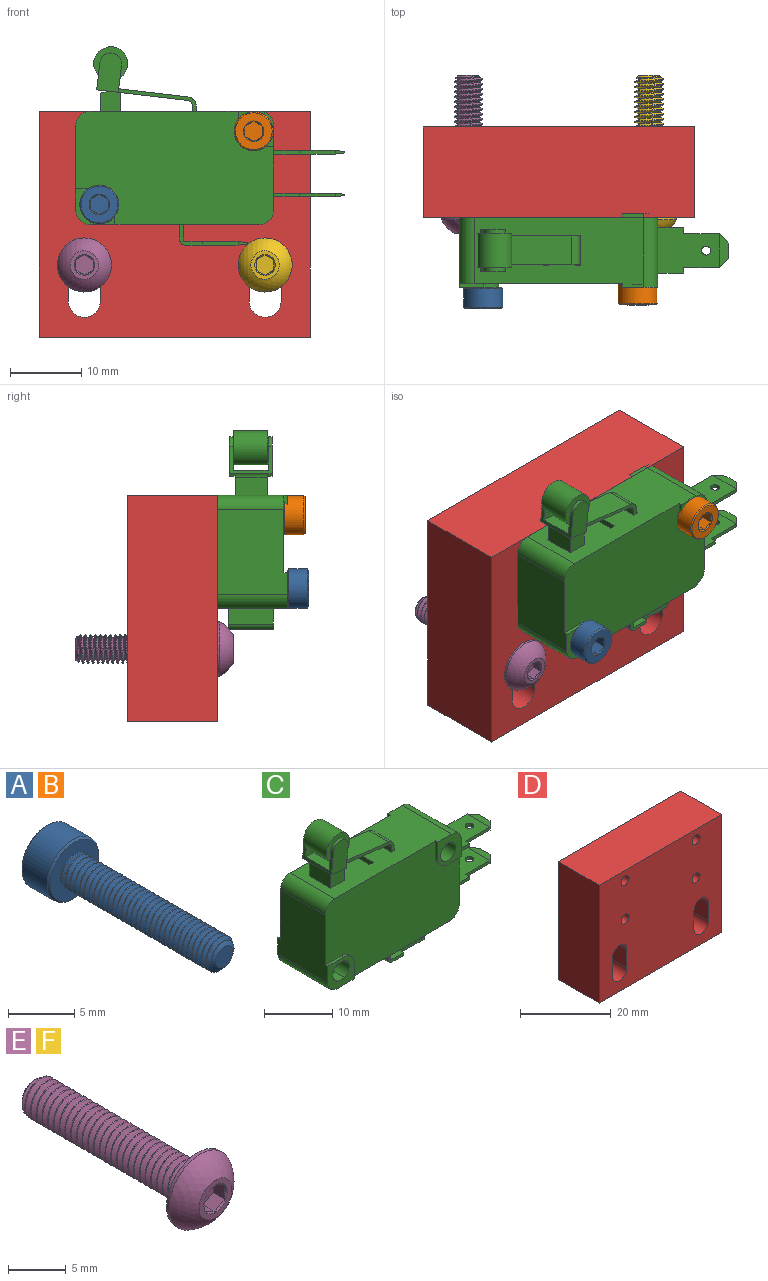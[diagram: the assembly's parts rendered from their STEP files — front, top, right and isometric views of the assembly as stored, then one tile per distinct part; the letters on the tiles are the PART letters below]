
ASSEMBLY  parts=6 mates=5
PART A: 57 faces, bbox 6x19.6x6 mm
  f0: cylinder r=1.5mm len=3mm, axis (0,-1,0), area 0.3mm2, adj f1,f32,f33,f35,f36
  f1: cylinder r=1.5mm len=3mm, axis (0,-1,0), area 0.6mm2, adj f0,f2,f32,f33
  f2: cylinder r=1.5mm len=3mm, axis (0,-1,0), area 0.6mm2, adj f1,f3,f32,f33
  f3: cylinder r=1.5mm len=3mm, axis (0,-1,0), area 0.6mm2, adj f2,f4,f32,f33
  f4: cylinder r=1.5mm len=3mm, axis (0,-1,0), area 0.6mm2, adj f3,f5,f32,f33
  f5: cylinder r=1.5mm len=3mm, axis (0,-1,0), area 0.6mm2, adj f4,f6,f32,f33
  f6: cylinder r=1.5mm len=3mm, axis (0,-1,0), area 0.6mm2, adj f5,f7,f32,f33
  f7: cylinder r=1.5mm len=3mm, axis (0,-1,0), area 0.6mm2, adj f6,f8,f32,f33
  f8: cylinder r=1.5mm len=3mm, axis (0,-1,0), area 0.6mm2, adj f7,f9,f32,f33
  f9: cylinder r=1.5mm len=3mm, axis (0,-1,0), area 0.6mm2, adj f8,f10,f32,f33
  f10: cylinder r=1.5mm len=3mm, axis (0,-1,0), area 0.6mm2, adj f9,f11,f32,f33
  f11: cylinder r=1.5mm len=3mm, axis (0,-1,0), area 0.6mm2, adj f10,f12,f32,f33
  f12: cylinder r=1.5mm len=3mm, axis (0,-1,0), area 0.6mm2, adj f11,f13,f32,f33
  f13: cylinder r=1.5mm len=3mm, axis (0,-1,0), area 0.6mm2, adj f12,f14,f32,f33
  f14: cylinder r=1.5mm len=3mm, axis (0,-1,0), area 0.6mm2, adj f13,f15,f32,f33
  f15: cylinder r=1.5mm len=3mm, axis (0,-1,0), area 0.6mm2, adj f14,f16,f32,f33
  f16: cylinder r=1.5mm len=3mm, axis (0,-1,0), area 0.6mm2, adj f15,f17,f32,f33
  f17: cylinder r=1.5mm len=3mm, axis (0,-1,0), area 0.6mm2, adj f16,f18,f32,f33
  f18: cylinder r=1.5mm len=3mm, axis (0,-1,0), area 0.6mm2, adj f17,f19,f32,f33
  f19: cylinder r=1.5mm len=3mm, axis (0,-1,0), area 0.6mm2, adj f18,f20,f32,f33
  f20: cylinder r=1.5mm len=3mm, axis (0,-1,0), area 0.6mm2, adj f19,f21,f32,f33
  f21: cylinder r=1.5mm len=3mm, axis (0,-1,0), area 0.6mm2, adj f20,f22,f32,f33
  f22: cylinder r=1.5mm len=3mm, axis (0,-1,0), area 0.6mm2, adj f21,f23,f32,f33
  f23: cylinder r=1.5mm len=3mm, axis (0,-1,0), area 0.6mm2, adj f22,f24,f32,f33
  f24: cylinder r=1.5mm len=3mm, axis (0,-1,0), area 0.6mm2, adj f23,f25,f32,f33
  f25: cylinder r=1.5mm len=3mm, axis (0,-1,0), area 0.6mm2, adj f24,f26,f32,f33
  f26: cylinder r=1.5mm len=3mm, axis (0,-1,0), area 0.6mm2, adj f25,f27,f32,f33
  f27: cylinder r=1.5mm len=3mm, axis (0,-1,0), area 0.6mm2, adj f26,f28,f32,f33
  f28: cylinder r=1.5mm len=3mm, axis (0,-1,0), area 0.6mm2, adj f27,f29,f32,f33
  f29: cylinder r=1.5mm len=3mm, axis (0,-1,0), area 0.6mm2, adj f28,f30,f32,f33
  f30: cylinder r=1.5mm len=3mm, axis (0,-1,0), area 0.6mm2, adj f29,f31,f32,f33
  f31: cylinder r=1.5mm len=3mm, axis (0,-1,0), area 1.4mm2, adj f30,f32,f33,f40,f56
  f32: bspline ~16.1x3.46mm, area 97.9mm2, adj f0,f1,f2,f3,f4,f5,f6,f7
  f33: bspline ~15.85x3.46mm, area 97.9mm2, adj f0,f1,f2,f3,f4,f5,f6,f7
  f34: cylinder r=1.18mm len=15.56mm, axis (0,1,0), area 26.7mm2, adj f32,f33,f35,f56
  f35: cone r=0.92mm half-angle=55deg, axis (0,1,0), area 3.5mm2, adj f0,f32,f34,f36,f37
  f36: cone r=0.92mm half-angle=55deg, axis (0,1,0), area 0.1mm2, adj f0,f33,f35
  f37: plane 1.84x1.84mm, normal (0,-1,0), area 2.7mm2, adj f35
  f38: cylinder r=2.75mm len=5.5mm, axis (0,-1,0), area 46.1mm2, adj f54,f55
  f39: plane 5.17x5.17mm, normal (0,1,0), area 14.4mm2, adj f41,f42,f43,f44,f45,f46,f54
  f40: plane 5.17x5.17mm, normal (0,-1,0), area 13.9mm2, adj f31,f55
  f41: cone r=1.44mm half-angle=45deg, axis (0,1,0), area 0mm2, adj f39,f48
  f42: cone r=1.44mm half-angle=45deg, axis (0,1,0), area 0mm2, adj f39,f49
  f43: cone r=1.44mm half-angle=45deg, axis (0,1,0), area 0mm2, adj f39,f50
  f44: cone r=1.44mm half-angle=45deg, axis (0,1,0), area 0mm2, adj f39,f51
  f45: cone r=1.44mm half-angle=45deg, axis (0,1,0), area 0mm2, adj f39,f52
  f46: cone r=1.44mm half-angle=45deg, axis (0,1,0), area 0mm2, adj f39,f53
  f47: plane 2.89x2.5mm, normal (0,1,0), area 5.4mm2, adj f48,f49,f50,f51,f52,f53
  f48: plane 2.42x1.8mm, normal (-0.5,0,-0.87), area 2.5mm2, adj f41,f47,f49,f53
  f49: plane 2.42x1.99mm, normal (-1,0,0), area 2.5mm2, adj f42,f47,f48,f50
  f50: plane 2.42x1.8mm, normal (-0.5,0,0.87), area 2.5mm2, adj f43,f47,f49,f51
  f51: plane 2.42x1.8mm, normal (0.5,0,0.87), area 2.5mm2, adj f44,f47,f50,f52
  f52: plane 2.42x1.99mm, normal (1,0,0), area 2.5mm2, adj f45,f47,f51,f53
  f53: plane 2.42x1.8mm, normal (0.5,0,-0.87), area 2.5mm2, adj f46,f47,f48,f52
  f54: cone r=2.58mm half-angle=45deg, axis (0,-1,0), area 3.9mm2, adj f38,f39
  f55: cone r=2.75mm half-angle=45deg, axis (0,1,0), area 3.9mm2, adj f38,f40
  f56: cone r=1.5mm half-angle=67.5deg, axis (0,1,0), area 1.5mm2, adj f31,f32,f33,f34
PART B: same geometry as A
PART C: 124 faces, bbox 37.8x10.3x27.9 mm
  f0: cylinder r=0.64mm len=1.27mm, axis (0,0,1), area 2mm2, adj f84,f85
  f1: cylinder r=0.64mm len=1.27mm, axis (0,0,1), area 2mm2, adj f73,f74
  f2: cylinder r=0.64mm len=1.27mm, axis (0,0,1), area 2mm2, adj f51,f53
  f3: cylinder r=1.7mm len=10.31mm, axis (0,1,0), area 40.2mm2, adj f6,f11,f13,f15
  f4: cylinder r=1.55mm len=10.31mm, axis (0,1,0), area 100.4mm2, adj f5,f12
  f5: plane 5x5mm, normal (0,1,0), area 15.6mm2, adj f4,f9,f10,f19,f42,f43,f44
  f6: plane 5.5x5mm, normal (0,1,0), area 16.8mm2, adj f3,f7,f8,f13,f14,f15,f16,f45
  f7: plane 11.9x10.31mm, normal (-1,0,0), area 113.8mm2, adj f6,f11,f16,f18,f37,f41,f45,f48
  f8: plane 23.8x10.31mm, normal (0,0,-1), area 221.9mm2, adj f6,f11,f16,f17,f35,f41,f47,f48
  f9: plane 11.9x10.31mm, normal (1,0,0), area 107.3mm2, adj f5,f12,f17,f19,f40,f41,f42,f48
  f10: plane 23.8x10.31mm, normal (0,0,1), area 205.5mm2, adj f5,f12,f18,f19,f20,f21,f22,f23
  f11: plane 5.5x5mm, normal (0,-1,0), area 16.8mm2, adj f3,f7,f8,f13,f14,f15,f16,f35
  f12: plane 5x5mm, normal (0,-1,0), area 15.6mm2, adj f4,f9,f10,f19,f38,f39,f40
  f13: plane 10.31x1.4mm, normal (0,0,1), area 14.4mm2, adj f3,f6,f11,f14
  f14: cylinder r=1.7mm len=10.31mm, axis (0,1,0), area 40.2mm2, adj f6,f11,f13,f15
  f15: plane 10.31x1.4mm, normal (0,0,-1), area 14.4mm2, adj f3,f6,f11,f14
  f16: cylinder r=2mm len=10.31mm, axis (0,1,0), area 32.4mm2, adj f6,f7,f8,f11
  f17: cylinder r=2mm len=9.31mm, axis (0,1,0), area 29.2mm2, adj f8,f9,f41,f48
  f18: cylinder r=2mm len=9.31mm, axis (0,1,0), area 29.2mm2, adj f7,f10,f41,f48
  f19: cylinder r=2mm len=10.31mm, axis (0,1,0), area 32.4mm2, adj f5,f9,f10,f12
  f20: plane 2.85x2mm, normal (0,1,0), area 4.4mm2, adj f10,f21,f23,f24,f115,f116,f117
  f21: plane 4.25x2mm, normal (1,0,0), area 8.5mm2, adj f10,f20,f22,f24
  f22: plane 2.85x2mm, normal (0,-1,0), area 5.7mm2, adj f10,f21,f23,f24
  f23: plane 4.25x2mm, normal (-1,0,0), area 8.5mm2, adj f10,f20,f22,f24
  f24: plane 4.25x2.85mm, normal (0,0,1), area 12.1mm2, adj f20,f21,f22,f23
  f25: plane 4.25x2mm, normal (1,0,0), area 8.5mm2, adj f10,f26,f28,f29
  f26: plane 2x0.76mm, normal (0,-1,0), area 1.5mm2, adj f10,f25,f27,f29
  f27: plane 4.25x2mm, normal (-1,0,0), area 8.5mm2, adj f10,f26,f28,f29
  f28: plane 2x0.76mm, normal (0,1,0), area 1.5mm2, adj f10,f25,f27,f29
  f29: plane 4.25x0.76mm, normal (0,0,1), area 3.2mm2, adj f25,f26,f27,f28
  f30: plane 4.25x2mm, normal (1,0,0), area 8.5mm2, adj f10,f31,f33,f34
  f31: plane 2x0.76mm, normal (0,-1,0), area 1.5mm2, adj f10,f30,f32,f34
  f32: plane 4.25x2mm, normal (-1,0,0), area 8.5mm2, adj f10,f31,f33,f34
  f33: plane 2x0.76mm, normal (0,1,0), area 1.5mm2, adj f10,f30,f32,f34
  f34: plane 4.25x0.76mm, normal (0,0,1), area 3.2mm2, adj f30,f31,f32,f33
  f35: plane 2.8x0.5mm, normal (1,0,0), area 1.4mm2, adj f8,f11,f36,f41
  f36: cylinder r=2.2mm len=2.2mm, axis (0,-1,0), area 1.7mm2, adj f11,f35,f37,f41
  f37: plane 3.3x0.5mm, normal (0,0,1), area 1.6mm2, adj f7,f11,f36,f41
  f38: plane 2.8x0.5mm, normal (-1,0,0), area 1.4mm2, adj f10,f12,f39,f41
  f39: cylinder r=2.2mm len=2.2mm, axis (0,-1,0), area 1.7mm2, adj f12,f38,f40,f41
  f40: plane 2.8x0.5mm, normal (0,0,-1), area 1.4mm2, adj f9,f12,f39,f41
  f41: plane 27.8x15.9mm, normal (0,-1,0), area 389.9mm2, adj f7,f8,f9,f10,f17,f18,f35,f36
  f42: plane 2.8x0.5mm, normal (0,0,-1), area 1.4mm2, adj f5,f9,f43,f48
  f43: cylinder r=2.2mm len=2.2mm, axis (0,1,0), area 1.7mm2, adj f5,f42,f44,f48
  f44: plane 2.8x0.5mm, normal (-1,0,0), area 1.4mm2, adj f5,f10,f43,f48
  f45: plane 3.3x0.5mm, normal (0,0,1), area 1.6mm2, adj f6,f7,f46,f48
  f46: cylinder r=2.2mm len=2.2mm, axis (0,1,0), area 1.7mm2, adj f6,f45,f47,f48
  f47: plane 2.8x0.5mm, normal (1,0,0), area 1.4mm2, adj f6,f8,f46,f48
  f48: plane 27.8x15.9mm, normal (0,1,0), area 389.9mm2, adj f7,f8,f9,f10,f17,f18,f42,f43
  f49: plane 6.35x2.19mm, normal (-1,0,0), area 13.9mm2, adj f8,f50,f56,f57
  f50: cylinder r=0.71mm len=6.35mm, axis (0,1,0), area 7.1mm2, adj f49,f51,f56,f57
  f51: plane 7.48x6.35mm, normal (0,0,-1), area 38.1mm2, adj f2,f50,f56,f57,f59,f60,f61,f63
  f52: plane 2.12x0.17mm, normal (1,0,0), area 0.4mm2, adj f58,f62,f86,f87
  f53: plane 7.48x6.35mm, normal (0,0,1), area 38.1mm2, adj f2,f54,f56,f57,f59,f60,f61,f63
  f54: cylinder r=0.2mm len=6.35mm, axis (0,1,0), area 2mm2, adj f53,f55,f56,f57
  f55: plane 6.35x2.19mm, normal (1,0,0), area 13.9mm2, adj f8,f54,f56,f57
  f56: plane 3.15x2.9mm, normal (0,-1,0), area 2.7mm2, adj f8,f49,f50,f51,f53,f54,f55,f63
  f57: plane 3.15x2.9mm, normal (0,1,0), area 2.7mm2, adj f8,f49,f50,f51,f53,f54,f55,f60
  f58: plane 1.32x1.32mm, normal (0.71,0.71,0), area 0.6mm2, adj f52,f59,f86,f87
  f59: plane 5.03x0.51mm, normal (0,1,0), area 2.6mm2, adj f51,f53,f58,f60
  f60: plane 0.8x0.51mm, normal (1,0,0), area 0.4mm2, adj f51,f53,f57,f59
  f61: plane 5.03x0.51mm, normal (0,-1,0), area 2.6mm2, adj f51,f53,f62,f63
  f62: plane 1.32x1.32mm, normal (0.71,-0.71,0), area 0.6mm2, adj f52,f61,f86,f87
  f63: plane 0.8x0.51mm, normal (1,0,0), area 0.4mm2, adj f51,f53,f56,f61
  f64: plane 3.65x0.51mm, normal (0,1,0), area 1.9mm2, adj f9,f65,f73,f74
  f65: plane 0.8x0.51mm, normal (1,0,0), area 0.4mm2, adj f64,f66,f73,f74
  f66: plane 5.03x0.51mm, normal (0,1,0), area 2.6mm2, adj f65,f67,f73,f74
  f67: plane 1.32x1.32mm, normal (0.71,0.71,0), area 0.6mm2, adj f66,f68,f88,f89
  f68: plane 2.12x0.17mm, normal (1,0,0), area 0.4mm2, adj f67,f69,f88,f89
  f69: plane 1.32x1.32mm, normal (0.71,-0.71,0), area 0.6mm2, adj f68,f70,f88,f89
  f70: plane 5.03x0.51mm, normal (0,-1,0), area 2.6mm2, adj f69,f71,f73,f74
  f71: plane 0.8x0.51mm, normal (1,0,0), area 0.4mm2, adj f70,f72,f73,f74
  f72: plane 3.65x0.51mm, normal (0,-1,0), area 1.9mm2, adj f9,f71,f73,f74
  f73: plane 8.68x6.35mm, normal (0,0,-1), area 45.8mm2, adj f1,f9,f64,f65,f66,f70,f71,f72
  f74: plane 8.68x6.35mm, normal (0,0,1), area 45.8mm2, adj f1,f9,f64,f65,f66,f70,f71,f72
  f75: plane 3.65x0.51mm, normal (0,1,0), area 1.9mm2, adj f9,f76,f84,f85
  f76: plane 0.8x0.51mm, normal (1,0,0), area 0.4mm2, adj f75,f77,f84,f85
  f77: plane 5.03x0.51mm, normal (0,1,0), area 2.6mm2, adj f76,f78,f84,f85
  f78: plane 1.32x1.32mm, normal (0.71,0.71,0), area 0.6mm2, adj f77,f79,f90,f91
  f79: plane 2.12x0.17mm, normal (1,0,0), area 0.4mm2, adj f78,f80,f90,f91
  f80: plane 1.32x1.32mm, normal (0.71,-0.71,0), area 0.6mm2, adj f79,f81,f90,f91
  f81: plane 5.03x0.51mm, normal (0,-1,0), area 2.6mm2, adj f80,f82,f84,f85
  f82: plane 0.8x0.51mm, normal (1,0,0), area 0.4mm2, adj f81,f83,f84,f85
  f83: plane 3.65x0.51mm, normal (0,-1,0), area 1.9mm2, adj f9,f82,f84,f85
  f84: plane 8.68x6.35mm, normal (0,0,-1), area 45.8mm2, adj f0,f9,f75,f76,f77,f81,f82,f83
  f85: plane 8.68x6.35mm, normal (0,0,1), area 45.8mm2, adj f0,f9,f75,f76,f77,f81,f82,f83
  f86: plane 4.75x1.32mm, normal (0.13,0,0.99), area 4.6mm2, adj f52,f53,f58,f62
  f87: plane 4.75x1.32mm, normal (0.13,0,-0.99), area 4.6mm2, adj f51,f52,f58,f62
  f88: plane 4.75x1.32mm, normal (0.13,0,0.99), area 4.6mm2, adj f67,f68,f69,f74
  f89: plane 4.75x1.32mm, normal (0.13,0,-0.99), area 4.6mm2, adj f67,f68,f69,f73
  f90: plane 4.75x1.32mm, normal (0.13,0,0.99), area 4.6mm2, adj f78,f79,f80,f85
  f91: plane 4.75x1.32mm, normal (0.13,0,-0.99), area 4.6mm2, adj f78,f79,f80,f84
  f92: plane 2.8x2.8mm, normal (0,-1,0), area 7.6mm2, adj f10,f93,f112,f113,f116,f117
  f93: plane 12.76x6mm, normal (-0.12,0,-0.99), area 53.8mm2, adj f92,f100,f101,f103,f104,f106,f108,f110
  f94: cylinder r=0.38mm len=0.76mm, axis (0,1,0), area 1.3mm2, adj f104,f107
  f95: cylinder r=1.52mm len=3.04mm, axis (0,-1,0), area 2.7mm2, adj f100,f103,f105,f106
  f96: plane 12.76x4.88mm, normal (0.12,0,0.99), area 54.7mm2, adj f99,f100,f105,f106,f107,f108,f110,f111
  f97: plane 4.06x0.51mm, normal (0,0,-1), area 2.1mm2, adj f98,f102,f110,f111
  f98: plane 4.06x1.21mm, normal (1,0,0), area 4.9mm2, adj f97,f99,f110,f111
  f99: cylinder r=1.3mm len=4.06mm, axis (0,1,0), area 7.7mm2, adj f96,f98,f110,f111
  f100: plane 6x3.83mm, normal (-0.99,0,0.12), area 6.8mm2, adj f93,f95,f96,f103,f104,f105,f107,f109
  f101: cylinder r=0.79mm len=4.06mm, axis (0,1,0), area 4.7mm2, adj f93,f102,f110,f111
  f102: plane 4.06x1.21mm, normal (-1,0,0), area 4.9mm2, adj f97,f101,f110,f111
  f103: plane 5.53x3.49mm, normal (0,-1,0), area 15.4mm2, adj f93,f95,f100,f106
  f104: plane 5.53x3.49mm, normal (0,1,0), area 15mm2, adj f93,f94,f100,f108,f109
  f105: plane 5.03x3.43mm, normal (0,1,0), area 12.9mm2, adj f95,f96,f100,f106,f123
  f106: plane 3.83x0.97mm, normal (0.99,0,-0.12), area 2.4mm2, adj f93,f95,f96,f103,f105,f111
  f107: plane 5.03x3.43mm, normal (0,-1,0), area 13.4mm2, adj f94,f96,f100,f108,f109
  f108: plane 3.83x0.97mm, normal (0.99,0,-0.12), area 2.4mm2, adj f93,f96,f104,f107,f109,f110
  f109: cylinder r=1.52mm len=3.04mm, axis (0,1,0), area 2.7mm2, adj f100,f104,f107,f108
  f110: plane 10.94x3.65mm, normal (0,1,0), area 6.4mm2, adj f93,f96,f97,f98,f99,f101,f102,f108
  f111: plane 10.94x3.65mm, normal (0,-1,0), area 6.4mm2, adj f93,f96,f97,f98,f99,f101,f102,f106
  f112: cylinder r=4mm len=4.4mm, axis (0,1,0), area 2.1mm2, adj f92,f93,f114,f116
  f113: cylinder r=4mm len=4.4mm, axis (0,1,0), area 6.2mm2, adj f92,f93,f114,f117
  f114: plane 3.25x2.8mm, normal (0,1,0), area 8.9mm2, adj f93,f112,f113,f115,f116,f117
  f115: plane 4.23x2.8mm, normal (0,0,-1), area 11.8mm2, adj f20,f114,f116,f117
  f116: plane 4.4x3mm, normal (1,0,0), area 13.1mm2, adj f10,f20,f92,f112,f114,f115
  f117: plane 4.4x3mm, normal (-1,0,0), area 13.1mm2, adj f10,f20,f92,f113,f114,f115
  f118: plane 0.71x0.71mm, normal (0,1,0), area 0.4mm2, adj f122
  f119: plane 4.8x4.8mm, normal (0,1,0), area 17.7mm2, adj f121,f122
  f120: plane 4.8x4.8mm, normal (0,-1,0), area 17.1mm2, adj f121,f123
  f121: cylinder r=2.4mm len=4.8mm, axis (0,1,0), area 72.4mm2, adj f119,f120
  f122: cylinder r=0.36mm len=0.71mm, axis (0,-1,0), area 1.3mm2, adj f118,f119
  f123: cylinder r=0.56mm len=1.12mm, axis (0,-1,0), area 0.1mm2, adj f105,f120
PART D: 18 faces, bbox 38.1x12.7x31.8 mm
  f0: plane 38.1x31.75mm, normal (0,-1,0), area 1112.5mm2, adj f2,f3,f4,f5,f6,f7,f8,f9
  f1: plane 38.1x31.75mm, normal (0,1,0), area 1112.5mm2, adj f2,f3,f4,f5,f6,f7,f8,f9
  f2: plane 31.75x12.7mm, normal (1,0,0), area 403.2mm2, adj f0,f1,f3,f5
  f3: plane 38.1x12.7mm, normal (0,0,1), area 483.9mm2, adj f0,f1,f2,f4
  f4: plane 31.75x12.7mm, normal (-1,0,0), area 403.2mm2, adj f0,f1,f3,f5
  f5: plane 38.1x12.7mm, normal (0,0,-1), area 483.9mm2, adj f0,f1,f2,f4
  f6: cylinder r=1.25mm len=12.7mm, axis (0,-1,0), area 99.7mm2, adj f0,f1
  f7: cylinder r=1.25mm len=12.7mm, axis (0,-1,0), area 99.7mm2, adj f0,f1
  f8: cylinder r=1.25mm len=12.7mm, axis (0,-1,0), area 99.7mm2, adj f0,f1
  f9: cylinder r=1.25mm len=12.7mm, axis (0,-1,0), area 99.7mm2, adj f0,f1
  f10: cylinder r=2.25mm len=12.7mm, axis (0,-1,0), area 89.8mm2, adj f0,f1,f11,f13
  f11: plane 12.7x5.08mm, normal (-1,0,0), area 64.5mm2, adj f0,f1,f10,f12
  f12: cylinder r=2.25mm len=12.7mm, axis (0,-1,0), area 89.8mm2, adj f0,f1,f11,f13
  f13: plane 12.7x5.08mm, normal (1,0,0), area 64.5mm2, adj f0,f1,f10,f12
  f14: cylinder r=2.25mm len=12.7mm, axis (0,-1,0), area 89.8mm2, adj f0,f1,f15,f17
  f15: plane 12.7x5.08mm, normal (-1,0,0), area 64.5mm2, adj f0,f1,f14,f16
  f16: cylinder r=2.25mm len=12.7mm, axis (0,-1,0), area 89.8mm2, adj f0,f1,f15,f17
  f17: plane 12.7x5.08mm, normal (1,0,0), area 64.5mm2, adj f0,f1,f14,f16
PART E: 23 faces, bbox 8.2x23.4x8.2 mm
  f0: cone r=1.44mm half-angle=45deg, axis (0,-1,0), area 0.2mm2, adj f9,f17
  f1: cylinder r=3.8mm len=7.6mm, axis (0,-1,0), area 7.9mm2, adj f2,f10
  f2: sphere r=4.23mm, area 49.8mm2, adj f1,f9
  f3: cone r=1.47mm half-angle=45deg, axis (0,-1,0), area 4.4mm2, adj f4,f5,f6,f7,f8
  f4: cylinder r=2mm len=19.48mm, axis (0,1,0), area 30.6mm2, adj f3,f6,f8,f10
  f5: plane 2.95x2.95mm, normal (0,1,0), area 6.8mm2, adj f3
  f6: bspline ~20.33x4.62mm, area 164.8mm2, adj f3,f4,f7,f10
  f7: bspline ~20.27x3.57mm, area 24.1mm2, adj f3,f6,f8,f10
  f8: bspline ~20.45x3.99mm, area 164.7mm2, adj f3,f4,f7,f10
  f9: plane 4.47x4.47mm, normal (0,-1,0), area 6mm2, adj f0,f2,f11,f12,f13,f14,f15
  f10: plane 7.87x7.87mm, normal (0,1,0), area 35.4mm2, adj f1,f4,f6,f7,f8
  f11: cone r=1.44mm half-angle=45deg, axis (0,-1,0), area 0mm2, adj f9,f18
  f12: cone r=1.44mm half-angle=45deg, axis (0,-1,0), area 0mm2, adj f9,f19
  f13: cone r=1.44mm half-angle=45deg, axis (0,-1,0), area 0mm2, adj f9,f20
  f14: cone r=1.44mm half-angle=45deg, axis (0,-1,0), area 0mm2, adj f9,f21
  f15: cone r=1.44mm half-angle=45deg, axis (0,-1,0), area 0mm2, adj f9,f22
  f16: plane 2.89x2.5mm, normal (0,-1,0), area 5.4mm2, adj f17,f18,f19,f20,f21,f22
  f17: plane 1.68x1.58mm, normal (-1,0,0), area 2mm2, adj f0,f16,f18,f22
  f18: plane 2.09x1.8mm, normal (-0.5,0,-0.87), area 2mm2, adj f11,f16,f17,f19
  f19: plane 2.09x1.8mm, normal (0.5,0,-0.87), area 2mm2, adj f12,f16,f18,f20
  f20: plane 2.09x1.99mm, normal (1,0,0), area 2mm2, adj f13,f16,f19,f21
  f21: plane 2.09x1.8mm, normal (0.5,0,0.87), area 2mm2, adj f14,f16,f20,f22
  f22: plane 2.09x1.8mm, normal (-0.5,0,0.87), area 2mm2, adj f15,f16,f17,f21
PART F: same geometry as E
PLACE A rot(axis=(1,0,0),180deg) t=(8.45,-6.51,18.66)mm
PLACE B rot(axis=(1,0,0),180deg) t=(30.15,-6.01,28.96)mm
PLACE C t=(19.05,-17.36,23.81)mm
PLACE D t=(19.05,-6.35,15.88)mm
PLACE E t=(6.35,-14.9,10.16)mm
PLACE F t=(31.75,-14.9,10.16)mm
MATE fastened E.f0 <-> D.f12  axis (0,1,0) through (6.35,-12.7,10.16)mm
MATE fastened A.f0 <-> C.f36  axis (0,1,0) through (8.45,-22.51,18.66)mm
MATE fastened B.f0 <-> C.f4  axis (0,1,0) through (30.15,-22.01,28.96)mm
MATE fastened D.f16 <-> F.f0  axis (0,-1,0) through (31.75,-12.7,10.16)mm
MATE fastened C.f4 <-> D.f7  axis (0,1,0) through (30.15,-12.7,28.96)mm
